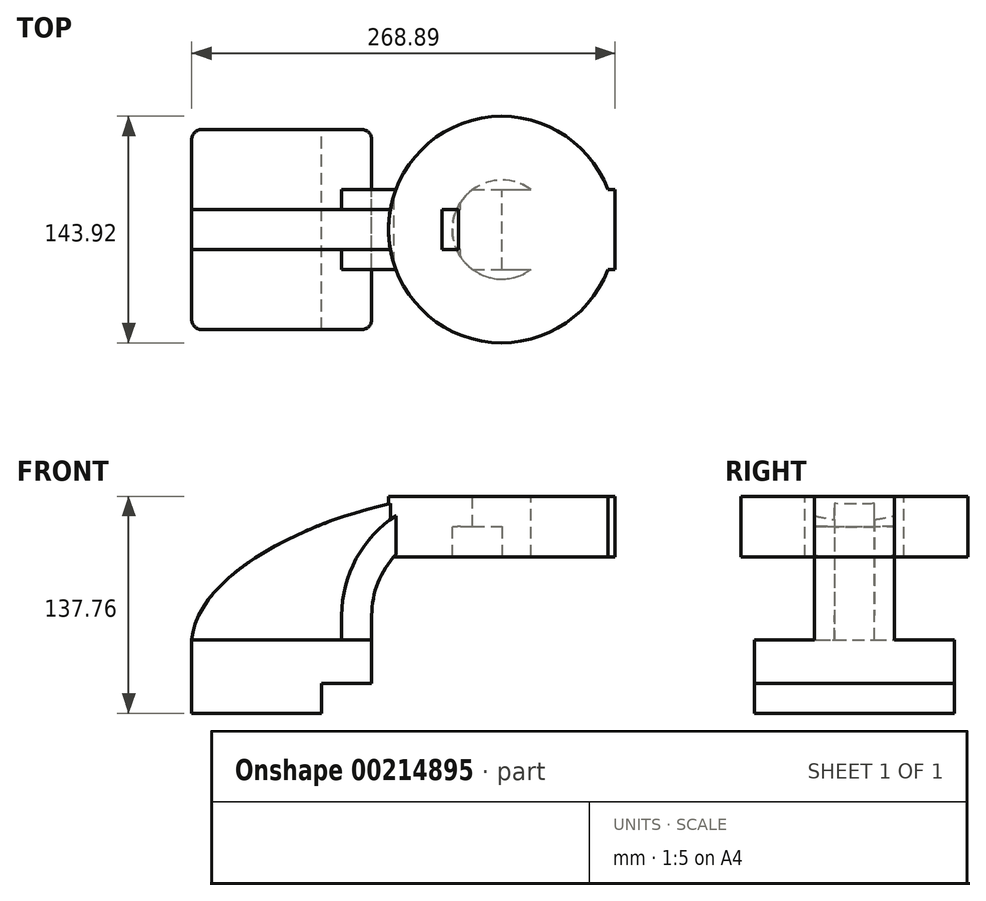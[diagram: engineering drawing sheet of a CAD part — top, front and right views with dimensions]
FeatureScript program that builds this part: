
annotation { "Feature Type Name" : "Feature", "Feature Type Description" : "" }
export const myFeature = defineFeature(function(context is Context, id is Id, definition is map)
    precondition{}
    {
        {
            var Q0;
            Q0=qCreatedBy(makeId("Front.planeOp"),FACE);
            var sketch = newSketch(context, id + "F0", { "sketchPlane" : qUnion([Q0])});
            skLineSegment(sketch, "E0.bottom", {"start": v(0, 0) * mm, "end": v(-82.55, 0) * mm});
            skLineSegment(sketch, "E0.top", {"start": v(0, 27.49) * mm, "end": v(-82.55, 27.49) * mm});
            skLineSegment(sketch, "E0.left", {"start": v(0, 0) * mm, "end": v(0, 27.49) * mm});
            skLineSegment(sketch, "E0.right", {"start": v(-82.55, 0) * mm, "end": v(-82.55, 27.49) * mm});
            skLineSegment(sketch, "E1.bottom", {"start": v(0, 0) * mm, "end": v(31.75, 0) * mm});
            skLineSegment(sketch, "E1.top", {"start": v(0, 27.49) * mm, "end": v(31.75, 27.49) * mm});
            skLineSegment(sketch, "E1.right", {"start": v(31.75, 0) * mm, "end": v(31.75, 27.49) * mm});
            skLineSegment(sketch, "E2.bottom", {"start": v(31.75, 0) * mm, "end": v(0, 0) * mm});
            skLineSegment(sketch, "E2.top", {"start": v(31.75, -19.05) * mm, "end": v(0, -19.05) * mm});
            skLineSegment(sketch, "E2.left", {"start": v(31.75, 0) * mm, "end": v(31.75, -19.05) * mm});
            skLineSegment(sketch, "E2.right", {"start": v(0, 0) * mm, "end": v(0, -19.05) * mm});
            skLineSegment(sketch, "E3.bottom", {"start": v(0, -19.05) * mm, "end": v(-82.55, -19.05) * mm});
            skLineSegment(sketch, "E3.left", {"start": v(0, -19.05) * mm, "end": v(0, 0) * mm});
            skLineSegment(sketch, "E3.right", {"start": v(-82.55, -19.05) * mm, "end": v(-82.55, 0) * mm});
            skLineSegment(sketch, "E4.bottom", {"start": v(114.39, 118.6) * mm, "end": v(186.34, 118.6) * mm});
            skLineSegment(sketch, "E4.top", {"start": v(114.39, 80.35) * mm, "end": v(186.34, 80.35) * mm});
            skLineSegment(sketch, "E4.left", {"start": v(114.39, 118.6) * mm, "end": v(114.39, 80.35) * mm});
            skLineSegment(sketch, "E4.right", {"start": v(186.34, 118.6) * mm, "end": v(186.34, 80.35) * mm});
            skLineSegment(sketch, "E5", {"start": v(31.75, 27.49) * mm, "end": v(31.75, 43.13) * mm});
            skArc(sketch, "E6", {"start": v(31.75, 43.13) * mm, "mid": v(48.25, 82.97) * mm, "end": v(88.1, 99.47) * mm});
            skLineSegment(sketch, "E7", {"start": v(88.1, 99.47) * mm, "end": v(145.29, 99.47) * mm});
            skPoint(sketch, "E7.endSnap0", {"position": v(114.39, 99.47) * mm});
            skLineSegment(sketch, "E8.0", {"start": v(88.1, 118.52) * mm, "end": v(145.82, 118.52) * mm});
            skArc(sketch, "E8.1", {"start": v(12.7, 43.13) * mm, "mid": v(34.78, 96.44) * mm, "end": v(88.1, 118.52) * mm});
            skLineSegment(sketch, "E8.2", {"start": v(12.7, 24.6) * mm, "end": v(12.7, 43.13) * mm});
            skLineSegment(sketch, "E9", {"start": v(145.82, 118.52) * mm, "end": v(145.82, 80.35) * mm});
            skFitSpline(sketch, "E10", {"points": [v(-82.55, 27.49) * mm, v(88.1, 118.52) * mm], "startDerivative": vector(12.15, 158.75) * mm, "endDerivative": vector(161.1, -9.93) * mm});
            skSolve(sketch);
        }
        {
            var Q0;
            Q0=makeQuery(id+"F0.imprint","IMPRINT",FACE,{"disambiguationData":[TD([[makeQuery(id+"F0.imprint","IMPRINT",EDGE,{"derivedFrom":sQuery(id+"F0.wireOp",EDGE,"E0.top")}),1.0]])]});
            var Q1;
            Q1=makeQuery(id+"F0.imprint","IMPRINT",FACE,{"disambiguationData":[TD([[makeQuery(id+"F0.imprint","IMPRINT",EDGE,{"derivedFrom":sQuery(id+"F0.wireOp",EDGE,"E1.top")}),-1.0]])]});
            var Q2;
            Q2=makeQuery(id+"F0.imprint","IMPRINT",FACE,{"disambiguationData":[TD([[makeQuery(id+"F0.imprint","IMPRINT",EDGE,{"derivedFrom":sQuery(id+"F0.wireOp",EDGE,"E2.bottom")}),1.0]])]});
            var Q3;
            Q3=makeQuery(id+"F0.imprint","IMPRINT",FACE,{"disambiguationData":[TD([[makeQuery(id+"F0.imprint","IMPRINT",EDGE,{"derivedFrom":sQuery(id+"F0.wireOp",EDGE,"E3.bottom")}),-1.0]])]});
            extrude(context, id + "F1", {"entities" : qUnion([Q0, Q1, Q2, Q3]), "endBound" : BoundingType.SYMMETRIC, "depth" : 127 * mm});
        }
        {
            var Q0;
            {var subQ0=sQuery(id+"F0.wireOp",EDGE,"E5");Q0=makeQuery(id+"F0.imprint","IMPRINT",FACE,{"disambiguationData":[TD([[makeQuery(id+"F0.imprint","IMPRINT",EDGE,{"derivedFrom":subQ0}),1.0]])]});}
            var Q1;
            {var subQ0=sQuery(id+"F0.wireOp",EDGE,"E4.left");var subQ1=sQuery(id+"F0.wireOp",EDGE,"E4.top");var subQ2=makeQuery(id+"F0.imprint","INTERSECT",VERTEX,{"derivedFrom":[subQ1,subQ0]});Q1=makeQuery(id+"F0.imprint","IMPRINT",FACE,{"disambiguationData":[TD([[makeQuery(id+"F0.imprint","IMPRINT",EDGE,{"disambiguationData":[TD([[subQ2,-1.0]])],"derivedFrom":subQ1}),1.0]])]});}
            var Q2;
            {var subQ0=sQuery(id+"F0.wireOp",EDGE,"E4.left");var subQ1=sQuery(id+"F0.wireOp",EDGE,"E4.bottom");var subQ2=makeQuery(id+"F0.imprint","INTERSECT",VERTEX,{"derivedFrom":[subQ1,subQ0]});Q2=makeQuery(id+"F0.imprint","IMPRINT",FACE,{"disambiguationData":[TD([[makeQuery(id+"F0.imprint","IMPRINT",EDGE,{"disambiguationData":[TD([[subQ2,-1.0]])],"derivedFrom":subQ1}),-1.0]])]});}
            var Q3;
            {var subQ0=sQuery(id+"F0.wireOp",EDGE,"E4.right");Q3=makeQuery(id+"F0.imprint","IMPRINT",FACE,{"disambiguationData":[TD([[makeQuery(id+"F0.imprint","IMPRINT",EDGE,{"derivedFrom":subQ0}),-1.0]])]});}
            extrude(context, id + "F2", {"entities" : qUnion([Q0, Q1, Q2, Q3]), "operationType" : NewBodyOperationType.ADD, "endBound" : BoundingType.SYMMETRIC, "depth" : 50.8 * mm});
        }
        {
            var Q0;
            {var subQ4=sQuery(id+"F0.wireOp",EDGE,"E0.top");Q0=makeQuery(id+"F0.imprint","IMPRINT",FACE,{"disambiguationData":[TD([[makeQuery(id+"F0.imprint","IMPRINT",EDGE,{"derivedFrom":subQ4}),-1.0]])]});}
            extrude(context, id + "F3", {"entities" : qUnion([Q0]), "operationType" : NewBodyOperationType.ADD, "endBound" : BoundingType.SYMMETRIC, "depth" : 25.4 * mm});
        }
        {
            var Q0;
            {var subQ2=sQuery(id+"F0.wireOp",EDGE,"E4.bottom");Q0=makeQuery(id+"F0.imprint","IMPRINT",FACE,{"disambiguationData":[TD([[makeQuery(id+"F0.imprint","IMPRINT",EDGE,{"derivedFrom":subQ2}),-1.0]])]});}
            var Q1;
            Q1=sQuery(id+"F0.wireOp",EDGE,"E4.left");
            revolve(context, id + "F4", {"operationType" : NewBodyOperationType.ADD, "entities" : qUnion([Q0]), "axis" : qUnion([Q1]), "revolveType" : RevolveType.FULL});
        }
        {
            var Q0;
            Q0=makeQuery(id+"F1.opExtrude","CAP_EDGE",EDGE,{"disambiguationData":[OSD([sQuery(id+"F0.wireOp",EDGE,"E0.right"),sQuery(id+"F0.wireOp",EDGE,"E3.right")])],"isStart":false});
            var Q1;
            Q1=makeQuery(id+"F1.opExtrude","CAP_EDGE",EDGE,{"disambiguationData":[OSD([sQuery(id+"F0.wireOp",EDGE,"E1.right"),sQuery(id+"F0.wireOp",EDGE,"E2.left")])],"isStart":false});
            var Q2;
            Q2=makeQuery(id+"F1.opExtrude","CAP_EDGE",EDGE,{"disambiguationData":[OSD([sQuery(id+"F0.wireOp",EDGE,"E1.right"),sQuery(id+"F0.wireOp",EDGE,"E2.left")])],"isStart":true});
            var Q3;
            Q3=makeQuery(id+"F1.opExtrude","CAP_EDGE",EDGE,{"disambiguationData":[OSD([sQuery(id+"F0.wireOp",EDGE,"E0.right"),sQuery(id+"F0.wireOp",EDGE,"E3.right")])],"isStart":true});
            fillet(context, id + "F5", {"entities" : qUnion([Q0, Q1, Q2, Q3]), "radius" : 6.35 * mm, "tangentPropagation" : true, "allowEdgeOverflow" : false});
        }
    });
